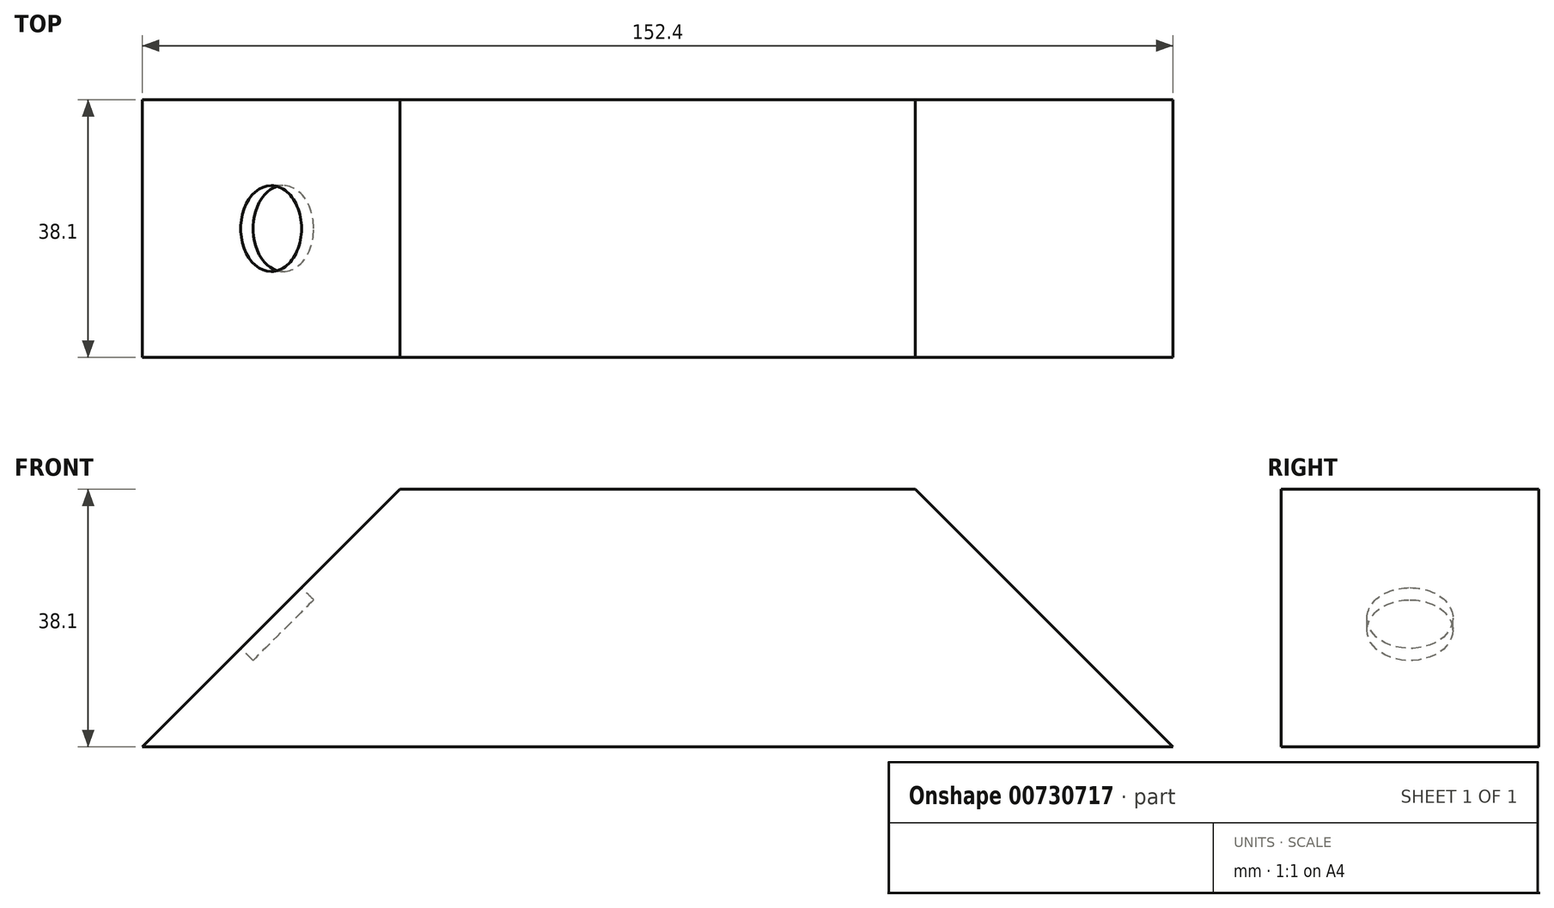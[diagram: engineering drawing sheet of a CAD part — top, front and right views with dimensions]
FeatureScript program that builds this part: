
annotation { "Feature Type Name" : "Feature", "Feature Type Description" : "" }
export const myFeature = defineFeature(function(context is Context, id is Id, definition is map)
    precondition{}
    {
        {
            var Q0;
            Q0=qCreatedBy(makeId("Top.planeOp"),FACE);
            var sketch = newSketch(context, id + "F0", { "sketchPlane" : qUnion([Q0])});
            skLineSegment(sketch, "E0.bottom", {"start": v(76.2, -19.05) * mm, "end": v(-76.2, -19.05) * mm});
            skLineSegment(sketch, "E0.top", {"start": v(76.2, 19.05) * mm, "end": v(-76.2, 19.05) * mm});
            skLineSegment(sketch, "E0.left", {"start": v(76.2, -19.05) * mm, "end": v(76.2, 19.05) * mm});
            skLineSegment(sketch, "E0.right", {"start": v(-76.2, -19.05) * mm, "end": v(-76.2, 19.05) * mm});
            skPoint(sketch, "E0.middle", {"position": v(0, 0) * mm});
            skSolve(sketch);
        }
        {
            var Q0;
            Q0 = qSketchRegion(id + "F0", true);
            extrude(context, id + "F1", {"entities" : qUnion([Q0]), "depth" : 38.1 * mm, "offsetDistance" : 25.4 * mm});
        }
        {
            var Q0;
            Q0=makeQuery(id+"F1.opExtrude","CAP_EDGE",EDGE,{"disambiguationData":[OSD([sQuery(id+"F0.wireOp",EDGE,"E0.right")])],"isStart":false});
            var Q1;
            Q1=makeQuery(id+"F1.opExtrude","CAP_EDGE",EDGE,{"disambiguationData":[OSD([sQuery(id+"F0.wireOp",EDGE,"E0.left")])],"isStart":false});
            chamfer(context, id + "F2", {"entities" : qUnion([Q0, Q1]), "width" : 38.1 * mm, "tangentPropagation" : true});
        }
        {
            var Q0;
            Q0=makeQuery(id+"F2.opChamfer","BLEND_FACE",FACE,{"disambiguationData":[OSD([sQuery(id+"F0.wireOp",EDGE,"E0.right")])]});
            var sketch = newSketch(context, id + "F3", { "sketchPlane" : qUnion([Q0])});
            skCircle(sketch, "E1", {"center": v(0, -26.94) * mm, "radius": 6.35 * mm});
            skPoint(sketch, "E1.centerSnap0", {"position": v(-19.05, -26.94) * mm});
            skSolve(sketch);
        }
        {
            var Q0;
            Q0 = qSketchRegion(id + "F3", true);
            extrude(context, id + "F4", {"entities" : qUnion([Q0]), "operationType" : NewBodyOperationType.REMOVE, "oppositeDirection" : true, "depth" : 2.54 * mm, "offsetDistance" : 25.4 * mm});
        }
    });
